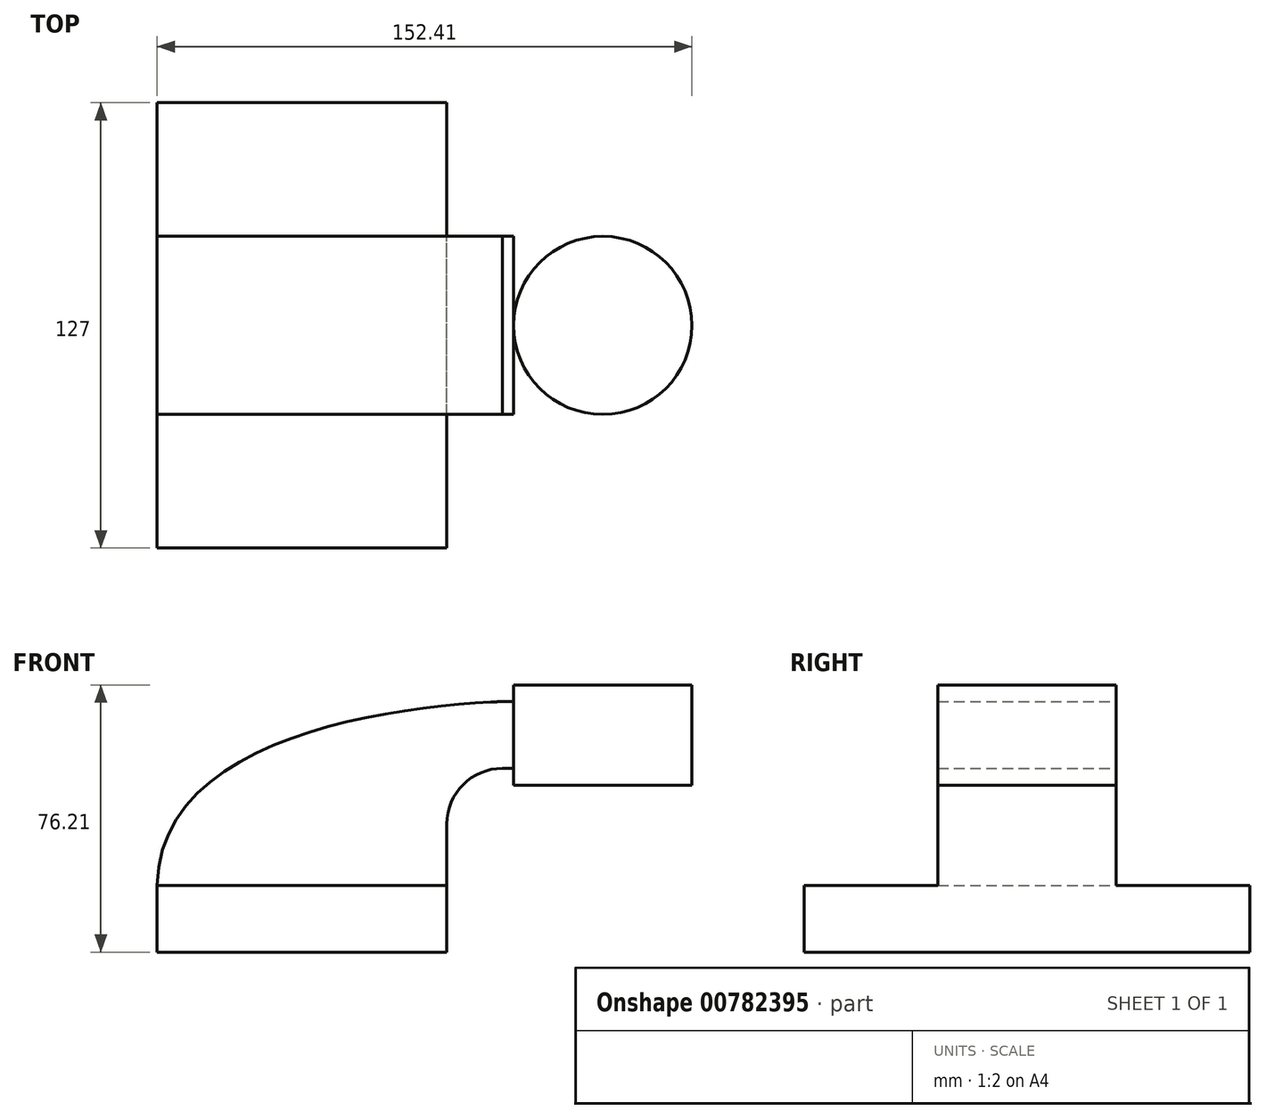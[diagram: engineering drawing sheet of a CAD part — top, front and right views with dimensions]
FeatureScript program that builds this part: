
annotation { "Feature Type Name" : "Feature", "Feature Type Description" : "" }
export const myFeature = defineFeature(function(context is Context, id is Id, definition is map)
    precondition{}
    {
        {
            var Q0;
            Q0=qCreatedBy(makeId("Front.planeOp"),FACE);
            var sketch = newSketch(context, id + "F0", { "sketchPlane" : qUnion([Q0])});
            skLineSegment(sketch, "E0.bottom", {"start": v(41.27, 9.53) * mm, "end": v(-41.28, 9.53) * mm});
            skLineSegment(sketch, "E0.top", {"start": v(41.28, -9.52) * mm, "end": v(-41.27, -9.52) * mm});
            skLineSegment(sketch, "E0.left", {"start": v(41.28, 9.53) * mm, "end": v(41.28, -9.52) * mm});
            skLineSegment(sketch, "E0.right", {"start": v(-41.28, 9.53) * mm, "end": v(-41.27, -9.52) * mm});
            skPoint(sketch, "E0.middle", {"position": v(0, 0) * mm});
            skLineSegment(sketch, "E1.bottom", {"start": v(111.13, 66.68) * mm, "end": v(60.33, 66.68) * mm});
            skLineSegment(sketch, "E1.top", {"start": v(111.13, 38.1) * mm, "end": v(60.33, 38.1) * mm});
            skLineSegment(sketch, "E1.left", {"start": v(111.13, 66.68) * mm, "end": v(111.13, 38.1) * mm});
            skLineSegment(sketch, "E1.right", {"start": v(60.33, 66.68) * mm, "end": v(60.33, 38.1) * mm});
            skPoint(sketch, "E1.middle", {"position": v(85.73, 52.39) * mm});
            skLineSegment(sketch, "E2", {"start": v(41.27, 9.53) * mm, "end": v(41.27, 27) * mm});
            skArc(sketch, "E3", {"start": v(41.27, 27) * mm, "mid": v(45.92, 38.23) * mm, "end": v(57.15, 42.88) * mm});
            skLineSegment(sketch, "E4", {"start": v(57.15, 42.88) * mm, "end": v(81.46, 42.88) * mm});
            skLineSegment(sketch, "E5.0", {"start": v(57.15, 61.93) * mm, "end": v(81.46, 61.93) * mm});
            skArc(sketch, "E5.1", {"start": v(22.23, 27) * mm, "mid": v(32.45, 51.7) * mm, "end": v(57.15, 61.93) * mm});
            skLineSegment(sketch, "E5.2", {"start": v(22.22, 9.53) * mm, "end": v(22.22, 27) * mm});
            skLineSegment(sketch, "E6", {"start": v(85.73, 38.1) * mm, "end": v(85.73, 66.68) * mm});
            skFitSpline(sketch, "E7", {"points": [v(-41.28, 9.52) * mm, v(57.15, 61.93) * mm], "startDerivative": vector(2.6, 128.18) * mm, "endDerivative": vector(94.87, 4) * mm});
            skSolve(sketch);
        }
        {
            var Q0;
            Q0=makeQuery(id+"F0.imprint","IMPRINT",FACE,{"disambiguationData":[TD([[makeQuery(id+"F0.imprint","IMPRINT",EDGE,{"derivedFrom":sQuery(id+"F0.wireOp",EDGE,"E0.top")}),-1.0]])]});
            extrude(context, id + "F1", {"entities" : qUnion([Q0]), "endBound" : BoundingType.SYMMETRIC, "depth" : 127 * mm, "offsetDistance" : 25.4 * mm});
        }
        {
            var Q0;
            {var subQ1=sQuery(id+"F0.wireOp",EDGE,"E2");Q0=makeQuery(id+"F0.imprint","IMPRINT",FACE,{"disambiguationData":[TD([[makeQuery(id+"F0.imprint","IMPRINT",EDGE,{"derivedFrom":subQ1}),1.0]])]});}
            var Q1;
            {var subQ3=sQuery(id+"F0.wireOp",EDGE,"E5.2");Q1=makeQuery(id+"F0.imprint","IMPRINT",FACE,{"disambiguationData":[TD([[makeQuery(id+"F0.imprint","IMPRINT",EDGE,{"derivedFrom":subQ3}),1.0]])]});}
            extrude(context, id + "F2", {"entities" : qUnion([Q0, Q1]), "operationType" : NewBodyOperationType.ADD, "endBound" : BoundingType.SYMMETRIC, "depth" : 50.8 * mm, "offsetDistance" : 25.4 * mm});
        }
        {
            var Q0;
            {var subQ6=sQuery(id+"F0.wireOp",EDGE,"E6");Q0=makeQuery(id+"F0.imprint","IMPRINT",FACE,{"disambiguationData":[TD([[makeQuery(id+"F0.imprint","IMPRINT",EDGE,{"derivedFrom":subQ6}),1.0]])]});}
            var Q1;
            Q1=sQuery(id+"F0.wireOp",EDGE,"E6");
            revolve(context, id + "F3", {"operationType" : NewBodyOperationType.ADD, "surfaceOperationType" : NewSurfaceOperationType.NEW, "entities" : qUnion([Q0]), "axis" : qUnion([Q1]), "revolveType" : RevolveType.FULL});
        }
    });
